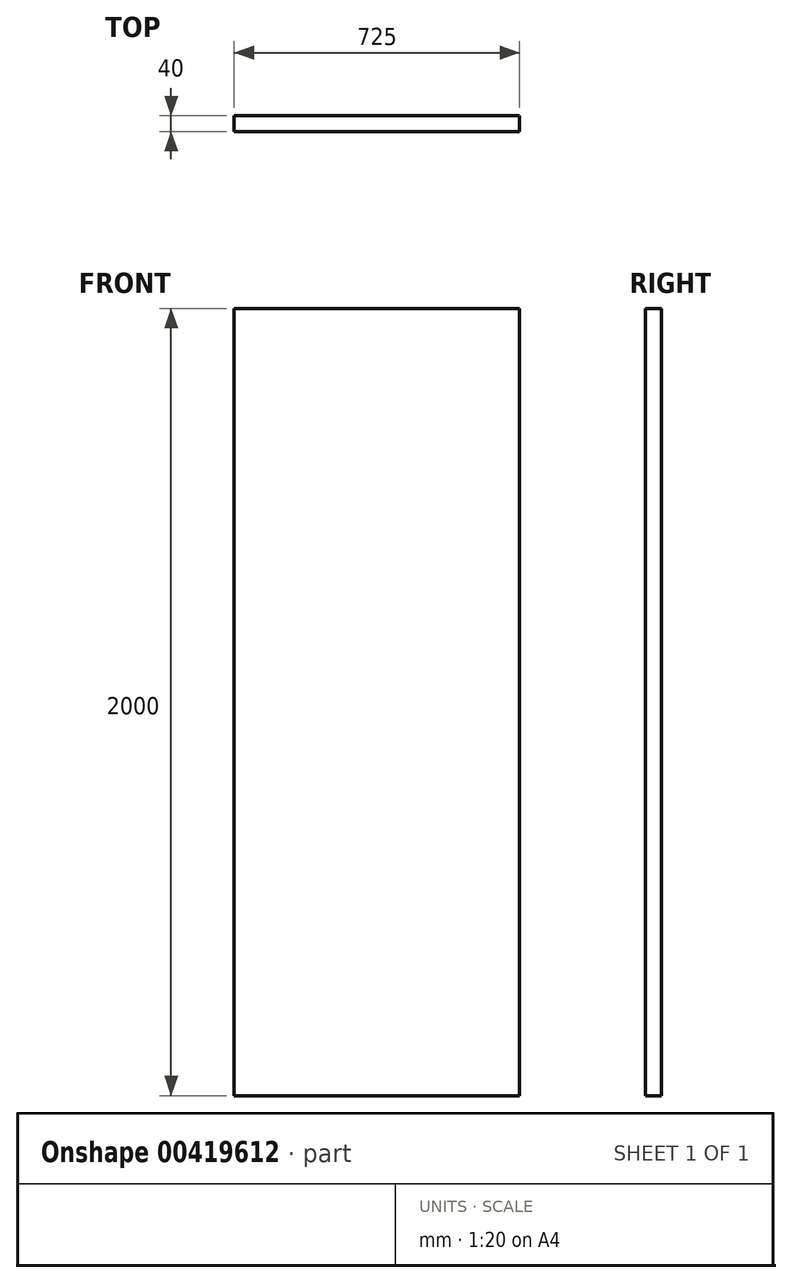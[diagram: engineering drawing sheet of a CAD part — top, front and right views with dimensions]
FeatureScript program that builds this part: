
annotation { "Feature Type Name" : "Feature", "Feature Type Description" : "" }
export const myFeature = defineFeature(function(context is Context, id is Id, definition is map)
    precondition{}
    {
        {
            var Q0;
            Q0=qCreatedBy(makeId("Top.planeOp"),FACE);
            var sketch = newSketch(context, id + "F0", { "sketchPlane" : qUnion([Q0])});
            skLineSegment(sketch, "E0.bottom", {"start": v(-596.92, 14.49) * mm, "end": v(128.08, 14.49) * mm});
            skLineSegment(sketch, "E0.top", {"start": v(-596.92, -25.51) * mm, "end": v(128.08, -25.51) * mm});
            skLineSegment(sketch, "E0.left", {"start": v(-596.92, 14.49) * mm, "end": v(-596.92, -25.51) * mm});
            skLineSegment(sketch, "E0.right", {"start": v(128.08, 14.49) * mm, "end": v(128.08, -25.51) * mm});
            skSolve(sketch);
        }
        {
            var Q0;
            Q0=makeQuery(id+"F0.imprint","IMPRINT",FACE,{"disambiguationData":[TD([[makeQuery(id+"F0.imprint","IMPRINT",EDGE,{"derivedFrom":sQuery(id+"F0.wireOp",EDGE,"E0.bottom")}),-1.0]])]});
            extrude(context, id + "F1", {"entities" : qUnion([Q0]), "depth" : 2000 * mm});
        }
    });
